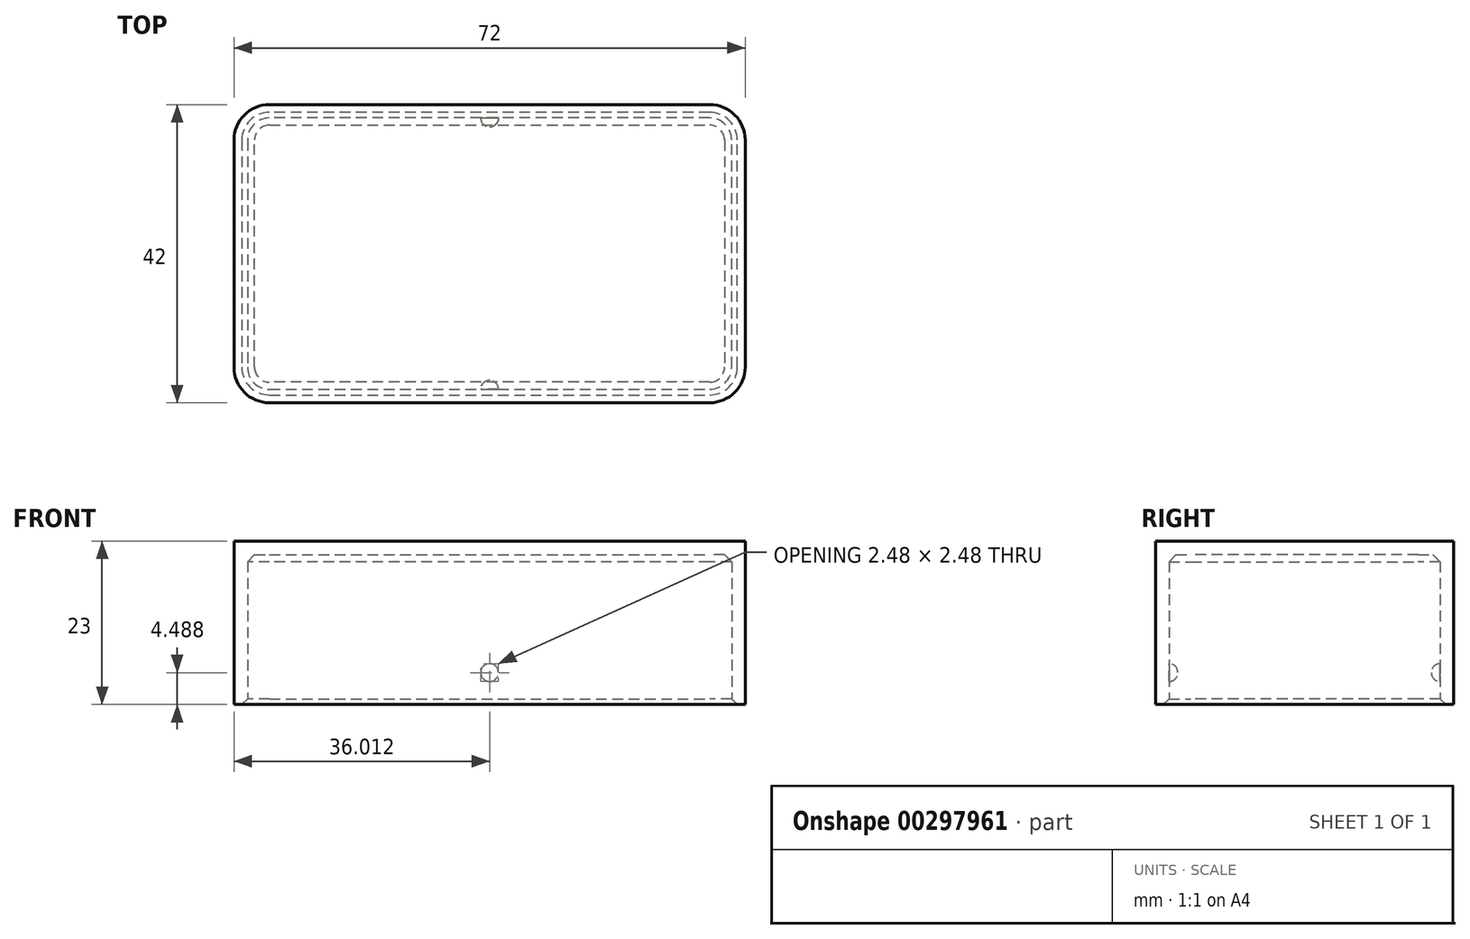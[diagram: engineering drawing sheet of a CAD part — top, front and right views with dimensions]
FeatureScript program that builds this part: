
annotation { "Feature Type Name" : "Feature", "Feature Type Description" : "" }
export const myFeature = defineFeature(function(context is Context, id is Id, definition is map)
    precondition{}
    {
        {
            var Q0;
            Q0=qCreatedBy(makeId("Top.planeOp"),FACE);
            var sketch = newSketch(context, id + "F0", { "sketchPlane" : qUnion([Q0])});
            skLineSegment(sketch, "E0.bottom", {"start": v(36, 21) * mm, "end": v(-36, 21) * mm});
            skLineSegment(sketch, "E0.top", {"start": v(36, -21) * mm, "end": v(-36, -21) * mm});
            skLineSegment(sketch, "E0.left", {"start": v(36, 21) * mm, "end": v(36, -21) * mm});
            skLineSegment(sketch, "E0.right", {"start": v(-36, 21) * mm, "end": v(-36, -21) * mm});
            skPoint(sketch, "E0.middle", {"position": v(0, 0) * mm});
            skSolve(sketch);
        }
        {
            var Q0;
            Q0=makeQuery(id+"F0.imprint","IMPRINT",FACE,{"disambiguationData":[TD([[makeQuery(id+"F0.imprint","IMPRINT",EDGE,{"derivedFrom":sQuery(id+"F0.wireOp",EDGE,"E0.bottom")}),1.0]])]});
            extrude(context, id + "F1", {"entities" : qUnion([Q0]), "depth" : 23 * mm});
        }
        {
            var Q0;
            Q0=makeQuery(id+"F1.opExtrude","SWEPT_EDGE",EDGE,{"disambiguationData":[OSD([sQuery(id+"F0.wireOp",EDGE,"E0.top"),sQuery(id+"F0.wireOp",EDGE,"E0.right")])]});
            var Q1;
            Q1=makeQuery(id+"F1.opExtrude","SWEPT_EDGE",EDGE,{"disambiguationData":[OSD([sQuery(id+"F0.wireOp",EDGE,"E0.top"),sQuery(id+"F0.wireOp",EDGE,"E0.left")])]});
            var Q2;
            Q2=makeQuery(id+"F1.opExtrude","SWEPT_EDGE",EDGE,{"disambiguationData":[OSD([sQuery(id+"F0.wireOp",EDGE,"E0.bottom"),sQuery(id+"F0.wireOp",EDGE,"E0.left")])]});
            var Q3;
            Q3=makeQuery(id+"F1.opExtrude","SWEPT_EDGE",EDGE,{"disambiguationData":[OSD([sQuery(id+"F0.wireOp",EDGE,"E0.bottom"),sQuery(id+"F0.wireOp",EDGE,"E0.right")])]});
            fillet(context, id + "F2", {"entities" : qUnion([Q0, Q1, Q2, Q3]), "radius" : 5 * mm, "tangentPropagation" : true, "allowEdgeOverflow" : false});
        }
        {
            var Q0;
            Q0=makeQuery(id+"F1.opExtrude","CAP_FACE",FACE,{"disambiguationData":[OSD([sQuery(id+"F0.wireOp",EDGE,"E0.bottom"),sQuery(id+"F0.wireOp",EDGE,"E0.top"),sQuery(id+"F0.wireOp",EDGE,"E0.left"),sQuery(id+"F0.wireOp",EDGE,"E0.right")])],"isStart":true});
            shell(context, id + "F3", {"entities" : qUnion([Q0]), "thickness" : 1.9 * mm});
        }
        {
            var Q0;
            {var subQ0=sQuery(id+"F0.wireOp",EDGE,"E0.right");var subQ1=sQuery(id+"F0.wireOp",EDGE,"E0.left");var subQ2=sQuery(id+"F0.wireOp",EDGE,"E0.top");var subQ3=sQuery(id+"F0.wireOp",EDGE,"E0.bottom");Q0=makeQuery(id+"F3.opShell","OFFSET_EDGE",EDGE,{"disambiguationData":[OSD([subQ3,subQ2,subQ1,subQ0]),TDD([makeQuery(id+"F2.opFillet","BLEND_EDGE",EDGE,{"blendedFrom":[makeQuery(id+"F1.opExtrude","SWEPT_EDGE",EDGE,{"disambiguationData":[OSD([subQ2,subQ1])]}),makeQuery(id+"F1.opExtrude","CAP_FACE",FACE,{"disambiguationData":[OSD([subQ3,subQ2,subQ1,subQ0])],"isStart":true})],"blendedInto":[makeQuery(id+"F1.opExtrude","CAP_FACE",FACE,{"disambiguationData":[OSD([subQ3,subQ2,subQ1,subQ0])],"isStart":true})]})])]});}
            chamfer(context, id + "F4", {"entities" : qUnion([Q0]), "width" : .8 * mm, "tangentPropagation" : true});
        }
        {
            var Q0;
            Q0=makeQuery(id+"F3.opShell","OFFSET_FACE",FACE,{"disambiguationData":[OSD([sQuery(id+"F0.wireOp",EDGE,"E0.bottom"),sQuery(id+"F0.wireOp",EDGE,"E0.top"),sQuery(id+"F0.wireOp",EDGE,"E0.left"),sQuery(id+"F0.wireOp",EDGE,"E0.right")])]});
            chamfer(context, id + "F5", {"entities" : qUnion([Q0]), "width" : 1 * mm, "tangentPropagation" : true});
        }
        {
            var Q0;
            Q0=makeQuery(id+"F1.opExtrude","CAP_FACE",FACE,{"disambiguationData":[OSD([sQuery(id+"F0.wireOp",EDGE,"E0.bottom"),sQuery(id+"F0.wireOp",EDGE,"E0.top"),sQuery(id+"F0.wireOp",EDGE,"E0.left"),sQuery(id+"F0.wireOp",EDGE,"E0.right")])],"isStart":true});
            cPlane(context, id + "F6", {"entities" : qUnion([Q0]), "cplaneType" : CPlaneType.OFFSET, "offset" : 4.5 * mm, "oppositeDirection" : true, "width" : 150 * mm, "height" : 150 * mm});
        }
        {
            var Q0;
            Q0=qCreatedBy(id+"F6.planeOp",FACE);
            var sketch = newSketch(context, id + "F7", { "sketchPlane" : qUnion([Q0])});
            skArc(sketch, "E1", {"start": v(1.25, -19.1) * mm, "mid": v(0.88, -18.22) * mm, "end": v(0, -17.85) * mm});
            skLineSegment(sketch, "E2", {"start": v(0, -17.85) * mm, "end": v(0, -19.1) * mm});
            skArc(sketch, "E3", {"start": v(-1.25, 19.1) * mm, "mid": v(-0.88, 18.22) * mm, "end": v(0, 17.85) * mm});
            skLineSegment(sketch, "E4", {"start": v(0, 17.85) * mm, "end": v(0, 19.1) * mm});
            skLineSegment(sketch, "E5", {"start": v(-1.25, 19.1) * mm, "end": v(0, 19.1) * mm});
            skLineSegment(sketch, "E6", {"start": v(0, -19.1) * mm, "end": v(1.25, -19.1) * mm});
            skSolve(sketch);
        }
        {
            var Q0;
            Q0 = qSketchRegion(id + "F7", true);
            var Q1;
            Q1=sQuery(id+"F7.wireOp",EDGE,"E2");
            revolve(context, id + "F8", {"operationType" : NewBodyOperationType.ADD, "entities" : qUnion([Q0]), "axis" : qUnion([Q1]), "revolveType" : RevolveType.FULL});
        }
    });
